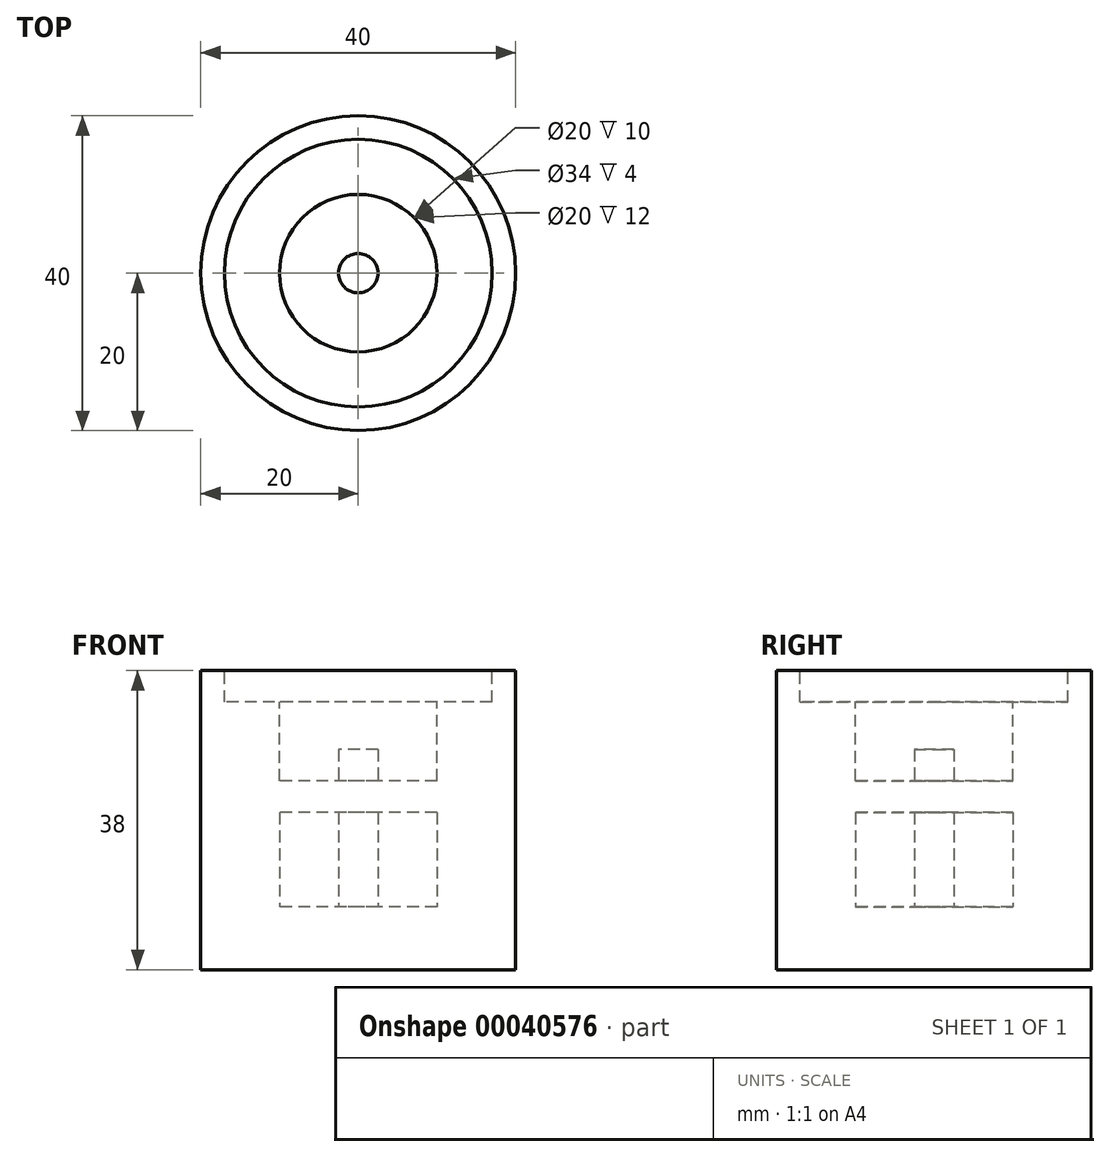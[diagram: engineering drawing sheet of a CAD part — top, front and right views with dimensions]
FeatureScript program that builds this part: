
annotation { "Feature Type Name" : "Feature", "Feature Type Description" : "" }
export const myFeature = defineFeature(function(context is Context, id is Id, definition is map)
    precondition{}
    {
        {
            var Q0;
            Q0=qCreatedBy(makeId("Top.planeOp"),FACE);
            var sketch = newSketch(context, id + "F0", { "sketchPlane" : qUnion([Q0])});
            skCircle(sketch, "E0", {"center": v(0, 0) * mm, "radius": 20 * mm});
            skCircle(sketch, "E1", {"center": v(0, 0) * mm, "radius": 10 * mm});
            skCircle(sketch, "E2", {"center": v(0, 0) * mm, "radius": 2.5 * mm});
            skSolve(sketch);
        }
        {
            var Q0;
            Q0=makeQuery(id+"F0.imprint","IMPRINT",FACE,{"disambiguationData":[TD([[makeQuery(id+"F0.imprint","IMPRINT",EDGE,{"derivedFrom":sQuery(id+"F0.wireOp",EDGE,"E0")}),1.0]])]});
            var Q1;
            Q1=makeQuery(id+"F0.imprint","IMPRINT",FACE,{"disambiguationData":[TD([[makeQuery(id+"F0.imprint","IMPRINT",EDGE,{"derivedFrom":sQuery(id+"F0.wireOp",EDGE,"E1")}),1.0]])]});
            extrude(context, id + "F1", {"entities" : qUnion([Q0, Q1]), "depth" : 38 * mm});
        }
        {
            var Q0;
            Q0=makeQuery(id+"F0.imprint","IMPRINT",FACE,{"disambiguationData":[TD([[makeQuery(id+"F0.imprint","IMPRINT",EDGE,{"derivedFrom":sQuery(id+"F0.wireOp",EDGE,"E1")}),1.0]])]});
            extrude(context, id + "F2", {"entities" : qUnion([Q0]), "operationType" : NewBodyOperationType.REMOVE, "depth" : 20 * mm});
        }
        {
            var Q0;
            Q0=makeQuery(id+"F1.opExtrude","CAP_FACE",FACE,{"disambiguationData":[OSD([sQuery(id+"F0.wireOp",EDGE,"E0"),sQuery(id+"F0.wireOp",EDGE,"E2")])],"isStart":false});
            var sketch = newSketch(context, id + "F3", { "sketchPlane" : qUnion([Q0])});
            skCircle(sketch, "E3.0", {"center": v(0, 0) * mm, "radius": 10 * mm});
            skCircle(sketch, "E4", {"center": v(0, 0) * mm, "radius": 17 * mm});
            skSolve(sketch);
        }
        {
            var Q0;
            Q0=makeQuery(id+"F3.imprint","IMPRINT",FACE,{"disambiguationData":[TD([[makeQuery(id+"F3.imprint","IMPRINT",EDGE,{"derivedFrom":sQuery(id+"F3.wireOp",EDGE,"E3.0")}),1.0]])]});
            extrude(context, id + "F4", {"entities" : qUnion([Q0]), "operationType" : NewBodyOperationType.REMOVE, "oppositeDirection" : true, "depth" : 14 * mm});
        }
        {
            var Q0;
            Q0=makeQuery(id+"F3.imprint","IMPRINT",FACE,{"disambiguationData":[TD([[makeQuery(id+"F3.imprint","IMPRINT",EDGE,{"derivedFrom":sQuery(id+"F3.wireOp",EDGE,"E3.0")}),-1.0]])]});
            extrude(context, id + "F5", {"entities" : qUnion([Q0]), "operationType" : NewBodyOperationType.REMOVE, "oppositeDirection" : true, "depth" : 4 * mm});
        }
        {
            var Q0;
            Q0=makeQuery(id+"F0.imprint","IMPRINT",FACE,{"disambiguationData":[TD([[makeQuery(id+"F0.imprint","IMPRINT",EDGE,{"derivedFrom":sQuery(id+"F0.wireOp",EDGE,"E1")}),1.0]])]});
            extrude(context, id + "F6", {"entities" : qUnion([Q0]), "depth" : 8 * mm});
        }
        {
            var Q0;
            Q0=makeQuery(id+"F0.imprint","IMPRINT",FACE,{"disambiguationData":[TD([[makeQuery(id+"F0.imprint","IMPRINT",EDGE,{"derivedFrom":sQuery(id+"F0.wireOp",EDGE,"E2")}),1.0]])]});
            extrude(context, id + "F7", {"entities" : qUnion([Q0]), "operationType" : NewBodyOperationType.ADD, "depth" : 28 * mm});
        }
    });
